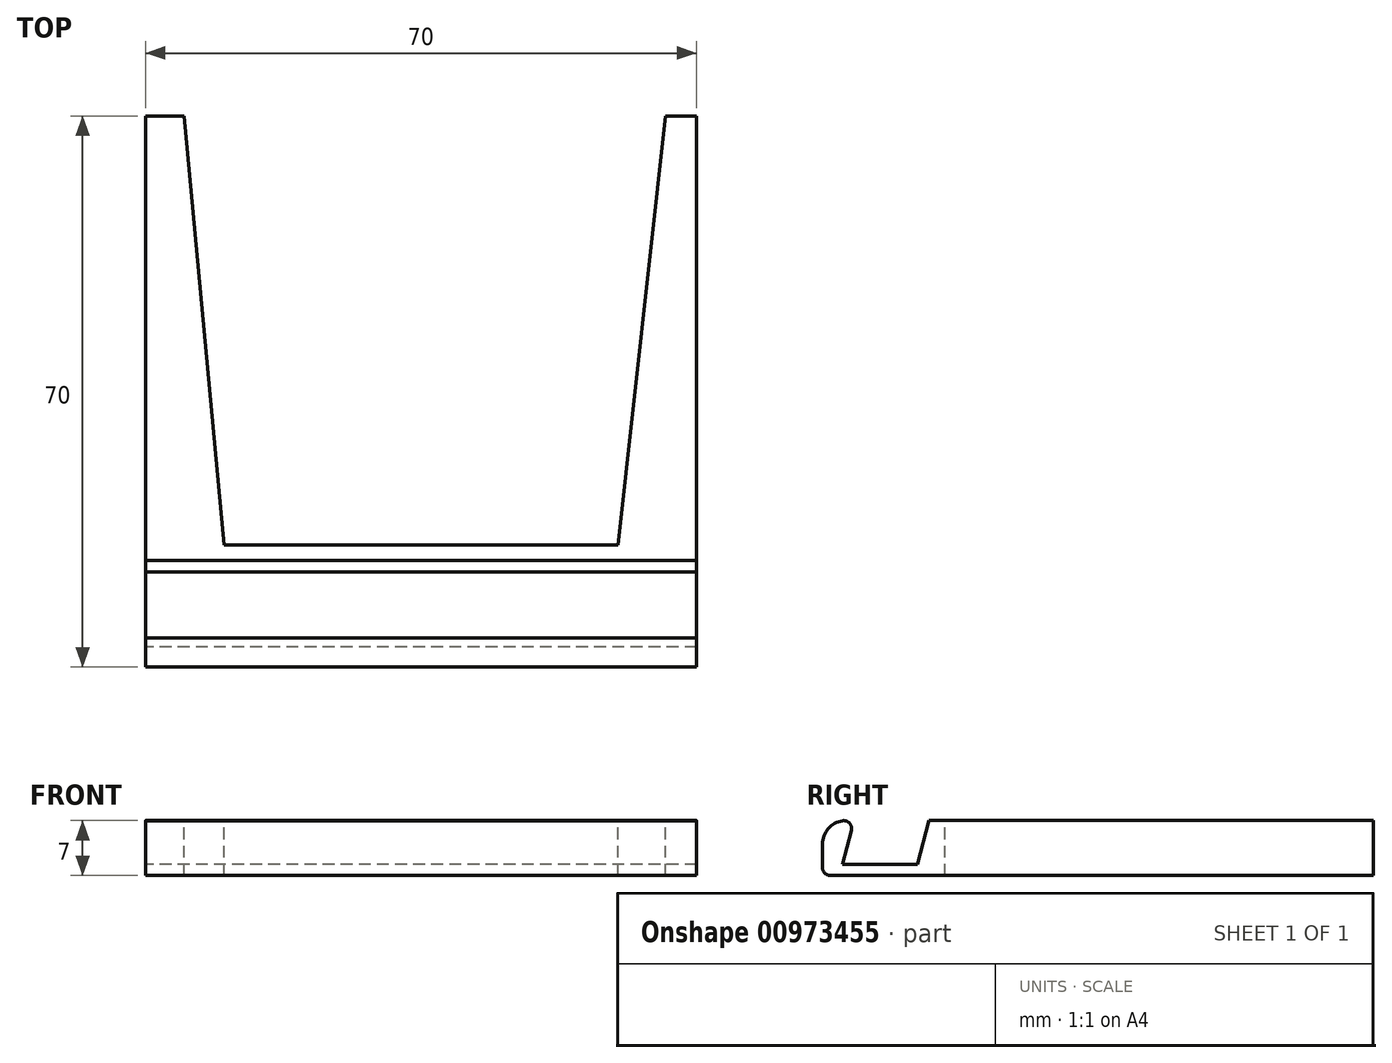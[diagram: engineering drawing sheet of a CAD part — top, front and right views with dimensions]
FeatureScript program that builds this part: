
annotation { "Feature Type Name" : "Feature", "Feature Type Description" : "" }
export const myFeature = defineFeature(function(context is Context, id is Id, definition is map)
    precondition{}
    {
        {
            var Q0;
            Q0=qCreatedBy(makeId("Top.planeOp"),FACE);
            var sketch = newSketch(context, id + "F0", { "sketchPlane" : qUnion([Q0])});
            skLineSegment(sketch, "E0.bottom", {"start": v(35, 35) * mm, "end": v(-35, 35) * mm});
            skLineSegment(sketch, "E0.top", {"start": v(35, -35) * mm, "end": v(-35, -35) * mm});
            skLineSegment(sketch, "E0.left", {"start": v(35, 35) * mm, "end": v(35, -35) * mm});
            skLineSegment(sketch, "E0.right", {"start": v(-35, 35) * mm, "end": v(-35, -35) * mm});
            skPoint(sketch, "E0.middle", {"position": v(0, 0) * mm});
            skSolve(sketch);
        }
        {
            var Q0;
            Q0=makeQuery(id+"F0.imprint","IMPRINT",FACE,{"disambiguationData":[TD([[makeQuery(id+"F0.imprint","IMPRINT",EDGE,{"derivedFrom":sQuery(id+"F0.wireOp",EDGE,"E0.bottom")}),1.0]])]});
            extrude(context, id + "F1", {"entities" : qUnion([Q0]), "depth" : 7 * mm, "offsetDistance" : 25 * mm});
        }
        {
            var Q0;
            Q0=makeQuery(id+"F1.opExtrude","SWEPT_FACE",FACE,{"disambiguationData":[OSD([sQuery(id+"F0.wireOp",EDGE,"E0.right")])]});
            var sketch = newSketch(context, id + "F2", { "sketchPlane" : qUnion([Q0])});
            skLineSegment(sketch, "E1", {"start": v(21.48, 7) * mm, "end": v(22.96, 1.45) * mm});
            skLineSegment(sketch, "E2", {"start": v(22.96, 1.45) * mm, "end": v(32.49, 1.45) * mm});
            skLineSegment(sketch, "E3", {"start": v(32.49, 1.45) * mm, "end": v(31, 7) * mm});
            skLineSegment(sketch, "E4", {"start": v(31, 7) * mm, "end": v(21.48, 7) * mm});
            skSolve(sketch);
        }
        {
            var Q0;
            Q0=makeQuery(id+"F2.imprint","IMPRINT",FACE,{"disambiguationData":[TD([[makeQuery(id+"F2.imprint","IMPRINT",EDGE,{"derivedFrom":sQuery(id+"F2.wireOp",EDGE,"E1")}),1.0]])]});
            extrude(context, id + "F3", {"entities" : qUnion([Q0]), "operationType" : NewBodyOperationType.REMOVE, "endBound" : BoundingType.UP_TO_NEXT, "oppositeDirection" : true, "depth" : 25 * mm, "offsetDistance" : 25 * mm});
        }
        {
            var Q0;
            Q0=makeQuery(id+"F1.opExtrude","CAP_EDGE",EDGE,{"disambiguationData":[OSD([sQuery(id+"F0.wireOp",EDGE,"E0.top")])],"isStart":false});
            fillet(context, id + "F4", {"entities" : qUnion([Q0]), "radius" : 3 * mm, "tangentPropagation" : true, "allowEdgeOverflow" : false});
        }
        {
            var Q0;
            Q0=makeQuery(id+"F1.opExtrude","CAP_EDGE",EDGE,{"disambiguationData":[OSD([sQuery(id+"F0.wireOp",EDGE,"E0.top")])],"isStart":true});
            fillet(context, id + "F5", {"entities" : qUnion([Q0]), "radius" : 1 * mm, "tangentPropagation" : true, "allowEdgeOverflow" : false});
        }
        {
            var Q0;
            Q0=makeQuery(id+"F3.boolean.opBoolean","COPY",EDGE,{"derivedFrom":makeQuery(id+"F3.opExtrude","SWEPT_EDGE",EDGE,{"disambiguationData":[OSD([sQuery(id+"F0.wireOp",EDGE,"E0.right"),sQuery(id+"F2.wireOp",EDGE,"E1"),sQuery(id+"F2.wireOp",EDGE,"E4")])]})});
            var Q1;
            Q1=makeQuery(id+"F3.boolean.opBoolean","COPY",EDGE,{"derivedFrom":makeQuery(id+"F3.opExtrude","SWEPT_EDGE",EDGE,{"disambiguationData":[OSD([sQuery(id+"F0.wireOp",EDGE,"E0.right"),sQuery(id+"F2.wireOp",EDGE,"E3"),sQuery(id+"F2.wireOp",EDGE,"E4")])]})});
            fillet(context, id + "F6", {"entities" : qUnion([Q0, Q1]), "radius" : 1 * mm, "tangentPropagation" : true, "allowEdgeOverflow" : false});
        }
        {
            var Q0;
            {var subQ0=sQuery(id+"F0.wireOp",EDGE,"E0.bottom");var subQ1=sQuery(id+"F0.wireOp",EDGE,"E0.right");var subQ2=sQuery(id+"F0.wireOp",EDGE,"E0.left");Q0=makeQuery(id+"F3.boolean.opBoolean","SPLIT",FACE,{"disambiguationData":[TD([makeQuery(id+"F1.opExtrude","SWEPT_FACE",FACE,{"disambiguationData":[OSD([subQ0])]})])],"derivedFrom":makeQuery(id+"F1.opExtrude","CAP_FACE",FACE,{"disambiguationData":[OSD([subQ0,sQuery(id+"F0.wireOp",EDGE,"E0.top"),subQ2,subQ1])],"isStart":false})});}
            var sketch = newSketch(context, id + "F7", { "sketchPlane" : qUnion([Q0])});
            skLineSegment(sketch, "E5.bottom", {"start": v(25, -19.48) * mm, "end": v(-25, -19.48) * mm});
            skPoint(sketch, "E5.middle", {"position": v(0, 35) * mm});
            skLineSegment(sketch, "E6", {"start": v(-25.1, 35) * mm, "end": v(26.08, 35) * mm});
            skPoint(sketch, "E7.orphan", {"position": v(-25, 89.48) * mm});
            skPoint(sketch, "E8.orphan", {"position": v(25, 89.48) * mm});
            skPoint(sketch, "E5.right.start.orphan", {"position": v(-25.21, -19.48) * mm});
            skPoint(sketch, "E5.left.start.orphan", {"position": v(27.16, -19.48) * mm});
            skLineSegment(sketch, "E9", {"start": v(-25, -19.48) * mm, "end": v(-30.1, 35) * mm});
            skLineSegment(sketch, "E10", {"start": v(-30.1, 35) * mm, "end": v(-25.1, 35) * mm});
            skLineSegment(sketch, "E11", {"start": v(25, -19.48) * mm, "end": v(31.08, 35) * mm});
            skLineSegment(sketch, "E12", {"start": v(31.08, 35) * mm, "end": v(26.08, 35) * mm});
            skSolve(sketch);
        }
        {
            var Q0;
            {var subQ0=sQuery(id+"F7.wireOp",EDGE,"E5.bottom");Q0=makeQuery(id+"F7.imprint","IMPRINT",FACE,{"disambiguationData":[TD([[makeQuery(id+"F7.imprint","IMPRINT",EDGE,{"derivedFrom":subQ0}),-1.0]])]});}
            extrude(context, id + "F8", {"entities" : qUnion([Q0]), "operationType" : NewBodyOperationType.REMOVE, "endBound" : BoundingType.UP_TO_NEXT, "oppositeDirection" : true, "depth" : 25 * mm, "offsetDistance" : 25 * mm});
        }
    });
